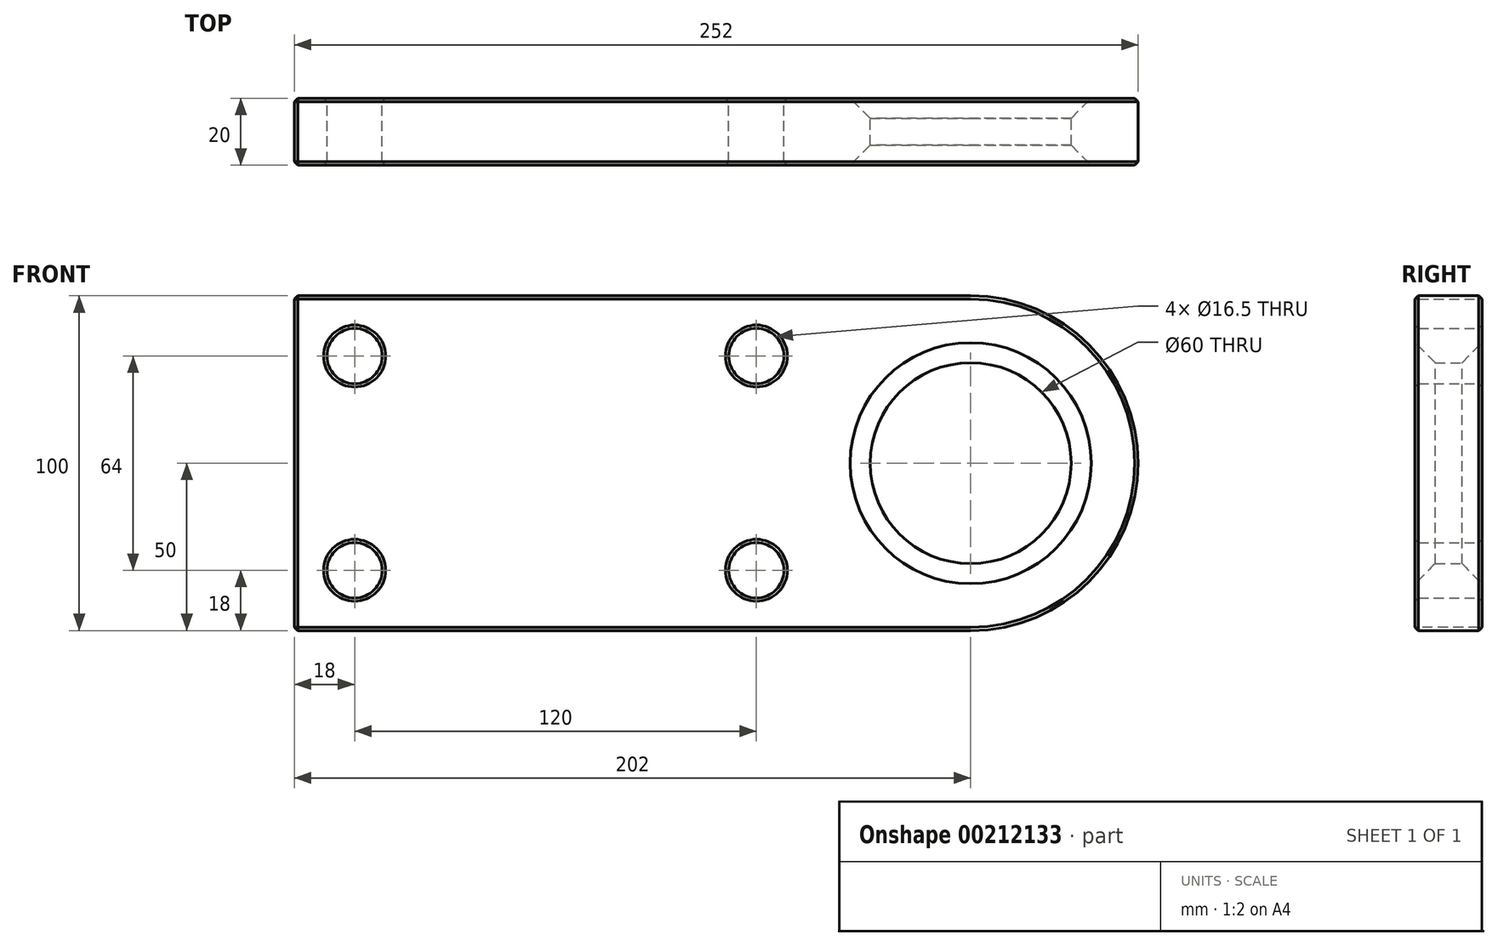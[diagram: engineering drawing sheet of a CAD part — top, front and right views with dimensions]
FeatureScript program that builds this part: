
annotation { "Feature Type Name" : "Feature", "Feature Type Description" : "" }
export const myFeature = defineFeature(function(context is Context, id is Id, definition is map)
    precondition{}
    {
        {
            var Q0;
            Q0=qCreatedBy(makeId("Front.planeOp"),FACE);
            var sketch = newSketch(context, id + "F0", { "sketchPlane" : qUnion([Q0])});
            skLineSegment(sketch, "E0.bottom", {"start": v(76, -50) * mm, "end": v(-126, -50) * mm});
            skLineSegment(sketch, "E0.top", {"start": v(76, 50) * mm, "end": v(-126, 50) * mm});
            skLineSegment(sketch, "E0.left", {"start": v(126, 0) * mm, "end": v(126, 0) * mm});
            skLineSegment(sketch, "E0.right", {"start": v(-126, -50) * mm, "end": v(-126, 50) * mm});
            skPoint(sketch, "E0.middle", {"position": v(0, 0) * mm});
            skPoint(sketch, "E1.visualSharp", {"position": v(126, 50) * mm});
            skArc(sketch, "E1.filletArc", {"start": v(126, 0) * mm, "mid": v(111.36, 35.36) * mm, "end": v(76, 50) * mm});
            skPoint(sketch, "E2.visualSharp", {"position": v(126, -50) * mm});
            skArc(sketch, "E2.filletArc", {"start": v(76, -50) * mm, "mid": v(111.36, -35.36) * mm, "end": v(126, 0) * mm});
            skCircle(sketch, "E3", {"center": v(-108, 32) * mm, "radius": 8.25 * mm});
            skCircle(sketch, "E4", {"center": v(-108, -32) * mm, "radius": 8.25 * mm});
            skCircle(sketch, "E5", {"center": v(12, -32) * mm, "radius": 8.25 * mm});
            skCircle(sketch, "E6", {"center": v(12, 32) * mm, "radius": 8.25 * mm});
            skCircle(sketch, "E7", {"center": v(76, 0) * mm, "radius": 30 * mm});
            skCircle(sketch, "E8", {"center": v(76, 0) * mm, "radius": 15.03 * mm});
            skSolve(sketch);
        }
        {
            var Q0;
            Q0=makeQuery(id+"F0.imprint","IMPRINT",FACE,{"disambiguationData":[TD([[makeQuery(id+"F0.imprint","IMPRINT",EDGE,{"derivedFrom":sQuery(id+"F0.wireOp",EDGE,"E0.bottom")}),-1.0]])]});
            extrude(context, id + "F1", {"entities" : qUnion([Q0]), "depth" : 20 * mm});
        }
        {
            var Q0;
            Q0=makeQuery(id+"F1.opExtrude","CAP_EDGE",EDGE,{"disambiguationData":[OSD([sQuery(id+"F0.wireOp",EDGE,"E7")])],"isStart":false});
            var Q1;
            Q1=makeQuery(id+"F1.opExtrude","CAP_EDGE",EDGE,{"disambiguationData":[OSD([sQuery(id+"F0.wireOp",EDGE,"E7")])],"isStart":true});
            chamfer(context, id + "F2", {"entities" : qUnion([Q0, Q1]), "width" : 6 * mm, "tangentPropagation" : true});
        }
        {
            var Q0;
            Q0=makeQuery(id+"F1.opExtrude","CAP_EDGE",EDGE,{"disambiguationData":[OSD([sQuery(id+"F0.wireOp",EDGE,"E4")])],"isStart":false});
            var Q1;
            Q1=makeQuery(id+"F1.opExtrude","CAP_EDGE",EDGE,{"disambiguationData":[OSD([sQuery(id+"F0.wireOp",EDGE,"E3")])],"isStart":false});
            var Q2;
            Q2=makeQuery(id+"F1.opExtrude","CAP_EDGE",EDGE,{"disambiguationData":[OSD([sQuery(id+"F0.wireOp",EDGE,"E5")])],"isStart":false});
            var Q3;
            Q3=makeQuery(id+"F1.opExtrude","CAP_EDGE",EDGE,{"disambiguationData":[OSD([sQuery(id+"F0.wireOp",EDGE,"E6")])],"isStart":false});
            var Q4;
            Q4=makeQuery(id+"F1.opExtrude","CAP_EDGE",EDGE,{"disambiguationData":[OSD([sQuery(id+"F0.wireOp",EDGE,"E0.bottom")])],"isStart":false});
            var Q5;
            Q5=makeQuery(id+"F1.opExtrude","CAP_EDGE",EDGE,{"disambiguationData":[OSD([sQuery(id+"F0.wireOp",EDGE,"E0.right")])],"isStart":false});
            var Q6;
            Q6=makeQuery(id+"F1.opExtrude","CAP_EDGE",EDGE,{"disambiguationData":[OSD([sQuery(id+"F0.wireOp",EDGE,"E0.top")])],"isStart":false});
            var Q7;
            Q7=makeQuery(id+"F1.opExtrude","CAP_EDGE",EDGE,{"disambiguationData":[OSD([sQuery(id+"F0.wireOp",EDGE,"E1.filletArc"),sQuery(id+"F0.wireOp",EDGE,"E2.filletArc")])],"isStart":false});
            var Q8;
            Q8=makeQuery(id+"F1.opExtrude","SWEPT_EDGE",EDGE,{"disambiguationData":[OSD([sQuery(id+"F0.wireOp",EDGE,"E0.bottom"),sQuery(id+"F0.wireOp",EDGE,"E0.right")])]});
            var Q9;
            Q9=makeQuery(id+"F1.opExtrude","CAP_EDGE",EDGE,{"disambiguationData":[OSD([sQuery(id+"F0.wireOp",EDGE,"E0.right")])],"isStart":true});
            var Q10;
            Q10=makeQuery(id+"F1.opExtrude","CAP_EDGE",EDGE,{"disambiguationData":[OSD([sQuery(id+"F0.wireOp",EDGE,"E0.bottom")])],"isStart":true});
            var Q11;
            Q11=makeQuery(id+"F1.opExtrude","CAP_EDGE",EDGE,{"disambiguationData":[OSD([sQuery(id+"F0.wireOp",EDGE,"E0.top")])],"isStart":true});
            var Q12;
            Q12=makeQuery(id+"F1.opExtrude","SWEPT_EDGE",EDGE,{"disambiguationData":[OSD([sQuery(id+"F0.wireOp",EDGE,"E0.top"),sQuery(id+"F0.wireOp",EDGE,"E0.right")])]});
            var Q13;
            Q13=makeQuery(id+"F1.opExtrude","CAP_EDGE",EDGE,{"disambiguationData":[OSD([sQuery(id+"F0.wireOp",EDGE,"E4")])],"isStart":true});
            var Q14;
            Q14=makeQuery(id+"F1.opExtrude","CAP_EDGE",EDGE,{"disambiguationData":[OSD([sQuery(id+"F0.wireOp",EDGE,"E3")])],"isStart":true});
            var Q15;
            Q15=makeQuery(id+"F1.opExtrude","CAP_EDGE",EDGE,{"disambiguationData":[OSD([sQuery(id+"F0.wireOp",EDGE,"E5")])],"isStart":true});
            var Q16;
            Q16=makeQuery(id+"F1.opExtrude","CAP_EDGE",EDGE,{"disambiguationData":[OSD([sQuery(id+"F0.wireOp",EDGE,"E6")])],"isStart":true});
            var Q17;
            Q17=makeQuery(id+"F1.opExtrude","CAP_EDGE",EDGE,{"disambiguationData":[OSD([sQuery(id+"F0.wireOp",EDGE,"E1.filletArc"),sQuery(id+"F0.wireOp",EDGE,"E2.filletArc")])],"isStart":true});
            chamfer(context, id + "F3", {"entities" : qUnion([Q0, Q1, Q2, Q3, Q4, Q5, Q6, Q7, Q8, Q9, Q10, Q11, Q12, Q13, Q14, Q15, Q16, Q17]), "width" : 1 * mm, "tangentPropagation" : true});
        }
    });
